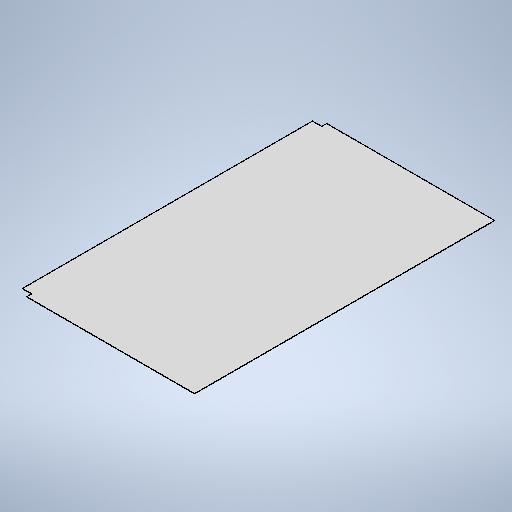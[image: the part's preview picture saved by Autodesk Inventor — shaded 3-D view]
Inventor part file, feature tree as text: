
AUTODESK INVENTOR PART (.ipt)
format: ipt  version: 2025.3 (Build 293356000, 356)  size: 295,424 bytes
history: native  units: mm
features: other x3, sketch x2, sheet_metal_op x1
ambient origin geometry x8: Origin, YZ Plane, XZ Plane, XY Plane, X Axis, Y Axis, Z Axis, Center Point
bodies: Solid1 (feature_tree)
feature tree (6):
  sheet_metal_op  "Face1"
  sketch  "Sketch1"  dims[d2=3.0mm]
  other  "Plate1"
  sketch  "Sketch5"  dims[d22=1240.0mm d23=2100.0mm d24=65.0mm d25=35.0mm d28=90.0mm d29=970.0mm d30=100.0mm d31=2.0mm d32=5.0mm d33=4.0mm d34=0.5mm d35=5.0mm d36=5.0mm d37=5.0mm d38=2.0mm d39=3.0mm d40=0.0mm]
  other  "Cut1"
  other  "Definition1"
